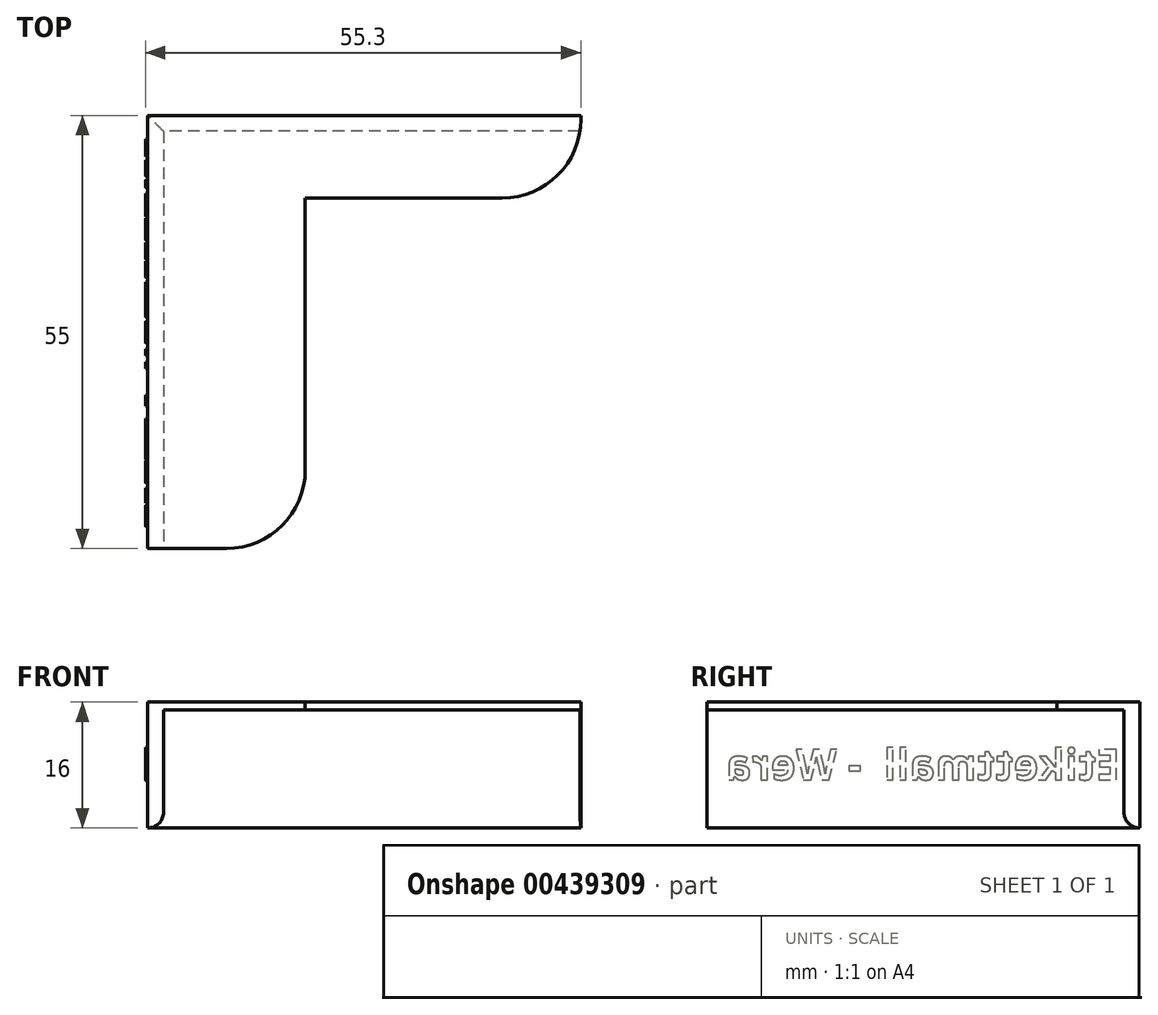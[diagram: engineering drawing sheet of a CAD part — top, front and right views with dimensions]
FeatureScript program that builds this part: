
annotation { "Feature Type Name" : "Feature", "Feature Type Description" : "" }
export const myFeature = defineFeature(function(context is Context, id is Id, definition is map)
    precondition{}
    {
        {
            var Q0;
            Q0=qCreatedBy(makeId("Top.planeOp"),FACE);
            var sketch = newSketch(context, id + "F0", { "sketchPlane" : qUnion([Q0])});
            skLineSegment(sketch, "E0.top", {"start": v(0, -44.5) * mm, "end": v(-20, -44.5) * mm});
            skLineSegment(sketch, "E0.left", {"start": v(0, 0) * mm, "end": v(0, -44.5) * mm});
            skLineSegment(sketch, "E0.right", {"start": v(-20, 0) * mm, "end": v(-20, -44.5) * mm});
            skLineSegment(sketch, "E1.bottom", {"start": v(0, 0) * mm, "end": v(35, 0) * mm});
            skLineSegment(sketch, "E1.top", {"start": v(-20, 10.5) * mm, "end": v(35, 10.5) * mm});
            skLineSegment(sketch, "E1.left", {"start": v(-20, 0) * mm, "end": v(-20, 10.5) * mm});
            skLineSegment(sketch, "E1.right", {"start": v(35, 0) * mm, "end": v(35, 10.5) * mm});
            skSolve(sketch);
        }
        {
            var Q0;
            Q0=makeQuery(id+"F0.imprint","IMPRINT",FACE,{"disambiguationData":[TD([[makeQuery(id+"F0.imprint","IMPRINT",EDGE,{"derivedFrom":sQuery(id+"F0.wireOp",EDGE,"E0.top")}),-1.0]])]});
            extrude(context, id + "F1", {"entities" : qUnion([Q0]), "depth" : 1 * mm});
        }
        {
            var Q0;
            Q0=makeQuery(id+"F1.opExtrude","CAP_FACE",FACE,{"disambiguationData":[OSD([sQuery(id+"F0.wireOp",EDGE,"E0.top"),sQuery(id+"F0.wireOp",EDGE,"E0.left"),sQuery(id+"F0.wireOp",EDGE,"E0.right"),sQuery(id+"F0.wireOp",EDGE,"E1.bottom"),sQuery(id+"F0.wireOp",EDGE,"E1.top"),sQuery(id+"F0.wireOp",EDGE,"E1.left"),sQuery(id+"F0.wireOp",EDGE,"E1.right")])],"isStart":true});
            var sketch = newSketch(context, id + "F2", { "sketchPlane" : qUnion([Q0])});
            skLineSegment(sketch, "E2.bottom", {"start": v(-20, -10.5) * mm, "end": v(-18, -10.5) * mm});
            skLineSegment(sketch, "E2.top", {"start": v(-20, 44.5) * mm, "end": v(-18, 44.5) * mm});
            skLineSegment(sketch, "E2.left", {"start": v(-20, -10.5) * mm, "end": v(-20, 44.5) * mm});
            skLineSegment(sketch, "E2.right", {"start": v(-18, -8.5) * mm, "end": v(-18, 44.5) * mm});
            skLineSegment(sketch, "E3.bottom", {"start": v(35, -10.5) * mm, "end": v(-18, -10.5) * mm});
            skLineSegment(sketch, "E3.top", {"start": v(35, -8.5) * mm, "end": v(-18, -8.5) * mm});
            skLineSegment(sketch, "E3.left", {"start": v(35, -10.5) * mm, "end": v(35, -8.5) * mm});
            skSolve(sketch);
        }
        {
            var Q0;
            Q0=makeQuery(id+"F2.imprint","IMPRINT",FACE,{"disambiguationData":[TD([[makeQuery(id+"F2.imprint","IMPRINT",EDGE,{"derivedFrom":sQuery(id+"F2.wireOp",EDGE,"E2.bottom")}),1.0]])]});
            extrude(context, id + "F3", {"entities" : qUnion([Q0]), "operationType" : NewBodyOperationType.ADD, "depth" : 15 * mm});
        }
        {
            var Q0;
            Q0=makeQuery(id+"F3.opExtrude","CAP_EDGE",EDGE,{"disambiguationData":[OSD([sQuery(id+"F2.wireOp",EDGE,"E2.right")])],"isStart":false});
            var Q1;
            Q1=makeQuery(id+"F3.opExtrude","CAP_EDGE",EDGE,{"disambiguationData":[OSD([sQuery(id+"F2.wireOp",EDGE,"E3.top")])],"isStart":false});
            fillet(context, id + "F4", {"entities" : qUnion([Q0, Q1]), "radius" : 2 * mm, "tangentPropagation" : true, "allowEdgeOverflow" : false});
        }
        {
            var Q0;
            Q0=makeQuery(id+"F1.opExtrude","SWEPT_EDGE",EDGE,{"disambiguationData":[OSD([sQuery(id+"F0.wireOp",EDGE,"E0.top"),sQuery(id+"F0.wireOp",EDGE,"E0.left")])]});
            var Q1;
            Q1=makeQuery(id+"F1.opExtrude","SWEPT_EDGE",EDGE,{"disambiguationData":[OSD([sQuery(id+"F0.wireOp",EDGE,"E1.bottom"),sQuery(id+"F0.wireOp",EDGE,"E1.right")])]});
            fillet(context, id + "F5", {"entities" : qUnion([Q0, Q1]), "radius" : 10 * mm, "tangentPropagation" : true, "allowEdgeOverflow" : false});
        }
        {
            var Q0;
            Q0=makeQuery(id+"F3.boolean.opBoolean","MERGE",FACE,{"derivedFrom":[makeQuery(id+"F1.opExtrude","SWEPT_FACE",FACE,{"disambiguationData":[OSD([sQuery(id+"F0.wireOp",EDGE,"E0.right"),sQuery(id+"F0.wireOp",EDGE,"E1.left")])]}),makeQuery(id+"F3.opExtrude","SWEPT_FACE",FACE,{"disambiguationData":[OSD([sQuery(id+"F2.wireOp",EDGE,"E2.left")])]})]});
            var sketch = newSketch(context, id + "F6", { "sketchPlane" : qUnion([Q0])});
            skText(sketch, "E4", { "text": "Etikettmall  - Wera", "fontName": "OpenSans-Bold.ttf"});
            skLineSegment(sketch, "E5", {"start": v(17, 1) * mm, "end": v(17, -15) * mm, "construction": true});
            const initialGuessF6  = {"E4": [-0.008, -0.00888, 1, 0, 0.00388]};
            skSetInitialGuess(sketch, initialGuessF6);
            skSolve(sketch);
        }
        {
            var Q0;
            Q0 = qSketchRegion(id + "F6", true);
            extrude(context, id + "F7", {"entities" : qUnion([Q0]), "operationType" : NewBodyOperationType.ADD, "depth" : 0.3 * mm, "offsetDistance" : 25 * mm});
        }
    });
